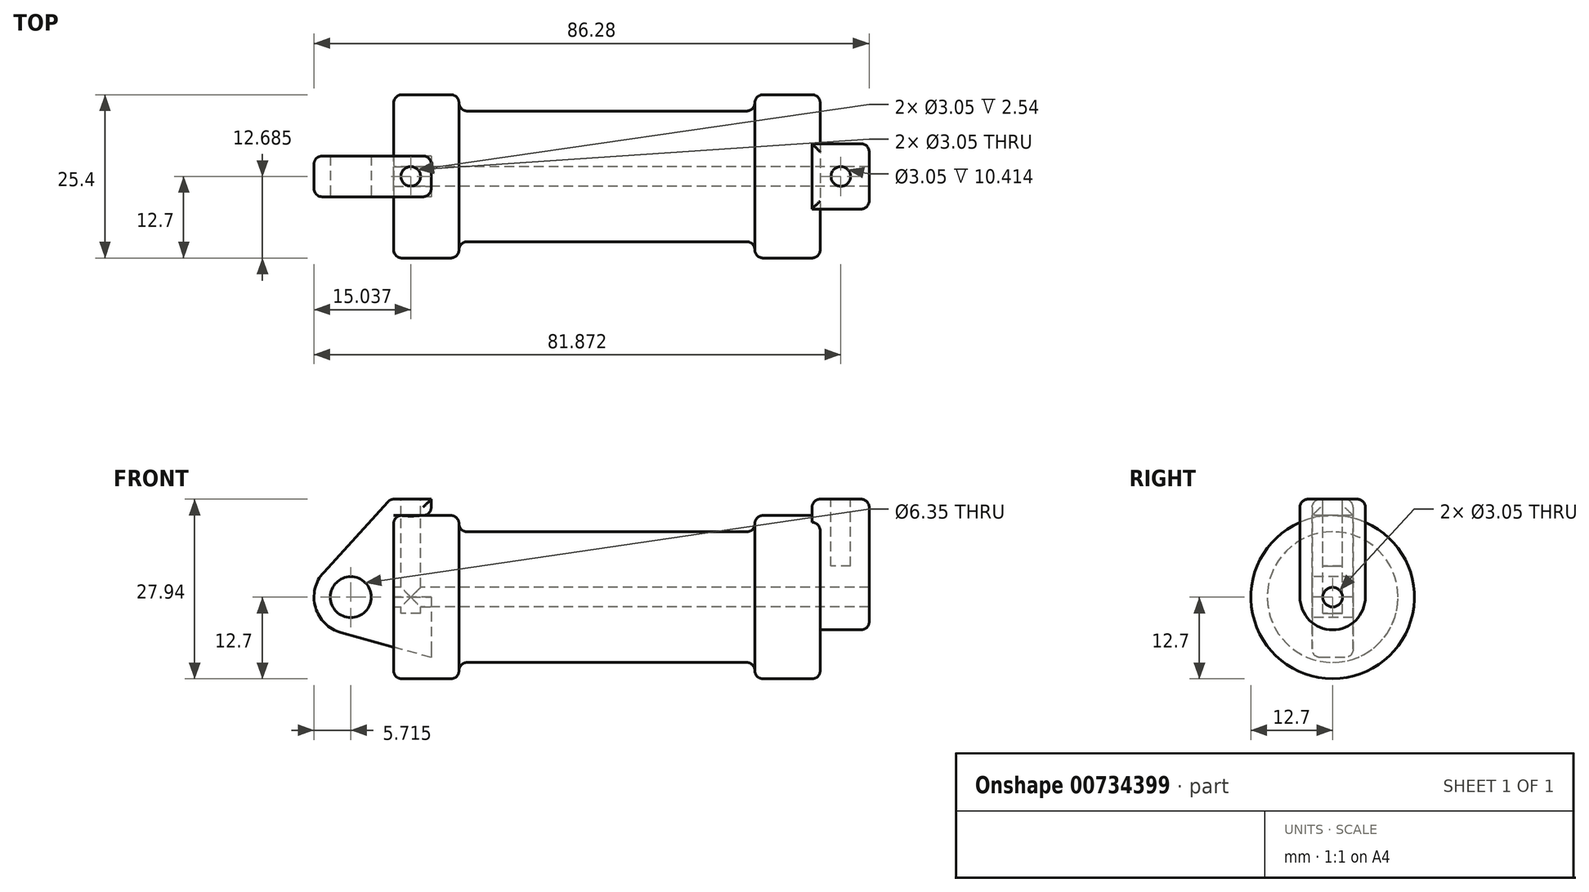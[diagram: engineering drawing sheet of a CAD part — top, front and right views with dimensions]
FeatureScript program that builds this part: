
annotation { "Feature Type Name" : "Feature", "Feature Type Description" : "" }
export const myFeature = defineFeature(function(context is Context, id is Id, definition is map)
    precondition{}
    {
        {
            var Q0;
            Q0=qCreatedBy(makeId("Front.planeOp"),FACE);
            var sketch = newSketch(context, id + "F0", { "sketchPlane" : qUnion([Q0])});
            skLineSegment(sketch, "E0", {"start": v(0, 0) * mm, "end": v(0, 12.7) * mm});
            skLineSegment(sketch, "E1", {"start": v(0, 12.7) * mm, "end": v(10.16, 12.7) * mm});
            skLineSegment(sketch, "E2", {"start": v(10.16, 12.7) * mm, "end": v(10.16, 10.16) * mm});
            skLineSegment(sketch, "E3", {"start": v(10.16, 10.16) * mm, "end": v(56.13, 10.16) * mm});
            skLineSegment(sketch, "E4", {"start": v(56.13, 10.16) * mm, "end": v(56.13, 12.7) * mm});
            skLineSegment(sketch, "E5", {"start": v(56.13, 12.7) * mm, "end": v(66.3, 12.7) * mm});
            skLineSegment(sketch, "E6", {"start": v(66.3, 12.7) * mm, "end": v(66.3, 0) * mm});
            skLineSegment(sketch, "E7", {"start": v(66.3, 0) * mm, "end": v(0, 0) * mm});
            skLineSegment(sketch, "E8", {"start": v(5.84, 15.24) * mm, "end": v(-0.5, 15.24) * mm});
            skLineSegment(sketch, "E9", {"start": v(-0.5, 15.24) * mm, "end": v(-10.88, 3.85) * mm});
            skLineSegment(sketch, "E10", {"start": v(0, 0) * mm, "end": v(-6.65, 0) * mm});
            skCircle(sketch, "E11", {"center": v(-6.65, 0) * mm, "radius": 5.72 * mm});
            skCircle(sketch, "E12", {"center": v(-6.65, 0) * mm, "radius": 3.18 * mm});
            skLineSegment(sketch, "E13", {"start": v(5.84, 15.24) * mm, "end": v(5.84, -9.4) * mm});
            skLineSegment(sketch, "E14", {"start": v(5.84, -9.4) * mm, "end": v(-8.18, -5.5) * mm});
            skSolve(sketch);
        }
        {
            var Q0;
            {var subQ0=sQuery(id+"F0.wireOp",EDGE,"E0");Q0=makeQuery(id+"F0.imprint","IMPRINT",FACE,{"disambiguationData":[TD([[makeQuery(id+"F0.imprint","IMPRINT",EDGE,{"derivedFrom":subQ0}),-1.0]])]});}
            var Q1;
            {var subQ0=sQuery(id+"F0.wireOp",EDGE,"E2");Q1=makeQuery(id+"F0.imprint","IMPRINT",FACE,{"disambiguationData":[TD([[makeQuery(id+"F0.imprint","IMPRINT",EDGE,{"derivedFrom":subQ0}),-1.0]])]});}
            var Q2;
            Q2=sQuery(id+"F0.wireOp",EDGE,"E7");
            revolve(context, id + "F1", {"surfaceOperationType" : NewSurfaceOperationType.NEW, "entities" : qUnion([Q0, Q1]), "axis" : qUnion([Q2]), "revolveType" : RevolveType.FULL});
        }
        {
            var Q0;
            {var subQ0=sQuery(id+"F0.wireOp",EDGE,"E14");Q0=makeQuery(id+"F0.imprint","IMPRINT",FACE,{"disambiguationData":[TD([[makeQuery(id+"F0.imprint","IMPRINT",EDGE,{"derivedFrom":subQ0}),-1.0]])]});}
            var Q1;
            {var subQ5=sQuery(id+"F0.wireOp",EDGE,"E12");Q1=makeQuery(id+"F0.imprint","IMPRINT",FACE,{"disambiguationData":[TD([[makeQuery(id+"F0.imprint","IMPRINT",EDGE,{"derivedFrom":subQ5}),-1.0]])]});}
            var Q2;
            {var subQ1=sQuery(id+"F0.wireOp",EDGE,"E0");Q2=makeQuery(id+"F0.imprint","IMPRINT",FACE,{"disambiguationData":[TD([[makeQuery(id+"F0.imprint","IMPRINT",EDGE,{"derivedFrom":subQ1}),1.0]])]});}
            extrude(context, id + "F2", {"entities" : qUnion([Q0, Q1, Q2]), "endBound" : BoundingType.SYMMETRIC, "oppositeDirection" : true, "depth" : 6.35 * mm, "offsetDistance" : 25.4 * mm});
        }
        {
            var Q0;
            Q0=makeQuery(id+"F1.opRevolve","SWEPT_FACE",FACE,{"disambiguationData":[OSD([sQuery(id+"F0.wireOp",EDGE,"E6")])]});
            var sketch = newSketch(context, id + "F3", { "sketchPlane" : qUnion([Q0])});
            skCircle(sketch, "E15", {"center": v(0, 0) * mm, "radius": 1.52 * mm});
            skCircle(sketch, "E16", {"center": v(0, 0) * mm, "radius": 5.08 * mm});
            skLineSegment(sketch, "E17", {"start": v(0, 0) * mm, "end": v(-5.08, 0) * mm});
            skLineSegment(sketch, "E18", {"start": v(-5.08, 0) * mm, "end": v(-5.08, 15.24) * mm});
            skLineSegment(sketch, "E19", {"start": v(5.08, 0) * mm, "end": v(5.08, 15.24) * mm});
            skLineSegment(sketch, "E20", {"start": v(-5.08, 15.24) * mm, "end": v(5.08, 15.24) * mm});
            skSolve(sketch);
        }
        {
            var Q0;
            {var subQ0=sQuery(id+"F3.wireOp",EDGE,"E20");Q0=makeQuery(id+"F3.imprint","IMPRINT",FACE,{"disambiguationData":[TD([[makeQuery(id+"F3.imprint","IMPRINT",EDGE,{"derivedFrom":subQ0}),-1.0]])]});}
            extrude(context, id + "F4", {"entities" : qUnion([Q0]), "operationType" : NewBodyOperationType.ADD, "oppositeDirection" : true, "depth" : 1.27 * mm, "offsetDistance" : 25.4 * mm});
        }
        {
            var Q0;
            Q0 = qSketchRegion(id + "F3", true);
            extrude(context, id + "F5", {"entities" : qUnion([Q0]), "operationType" : NewBodyOperationType.ADD, "depth" : 7.62 * mm, "offsetDistance" : 25.4 * mm});
        }
        {
            var Q0;
            {var subQ0=sQuery(id+"F0.wireOp",EDGE,"E6");Q0=makeQuery(id+"F5.boolean.opBoolean","SPLIT",FACE,{"disambiguationData":[TD([makeQuery(id+"F5.opExtrude","SWEPT_FACE",FACE,{"disambiguationData":[OSD([sQuery(id+"F3.wireOp",EDGE,"E15")])]})])],"derivedFrom":makeQuery(id+"F4.boolean.opBoolean","MERGE",FACE,{"derivedFrom":[makeQuery(id+"F1.opRevolve","SWEPT_FACE",FACE,{"disambiguationData":[OSD([subQ0])]}),makeQuery(id+"F4.opExtrude","CAP_FACE",FACE,{"disambiguationData":[OSD([sQuery(id+"F0.wireOp",EDGE,"E5"),subQ0,sQuery(id+"F3.wireOp",EDGE,"E18"),sQuery(id+"F3.wireOp",EDGE,"E19"),sQuery(id+"F3.wireOp",EDGE,"E20")])],"isStart":true})]})});}
            var Q1;
            Q1=makeQuery(id+"F1.opRevolve","SWEPT_BODY",BODY,{"disambiguationData":[OSD([sQuery(id+"F0.wireOp",EDGE,"E0"),sQuery(id+"F0.wireOp",EDGE,"E1"),sQuery(id+"F0.wireOp",EDGE,"E2"),sQuery(id+"F0.wireOp",EDGE,"E3"),sQuery(id+"F0.wireOp",EDGE,"E4"),sQuery(id+"F0.wireOp",EDGE,"E5"),sQuery(id+"F0.wireOp",EDGE,"E6"),sQuery(id+"F0.wireOp",EDGE,"E7")])]});
            extrude(context, id + "F6", {"entities" : qUnion([Q0]), "operationType" : NewBodyOperationType.REMOVE, "endBound" : BoundingType.UP_TO_BODY, "oppositeDirection" : true, "depth" : 25.4 * mm, "endBoundEntityBody" : qUnion([Q1]), "offsetDistance" : 25.4 * mm});
        }
        {
            var Q0;
            {var subQ0=sQuery(id+"F3.wireOp",EDGE,"E20");Q0=makeQuery(id+"F5.boolean.opBoolean","MERGE",FACE,{"derivedFrom":[makeQuery(id+"F4.opExtrude","SWEPT_FACE",FACE,{"disambiguationData":[OSD([subQ0])]}),makeQuery(id+"F5.opExtrude","SWEPT_FACE",FACE,{"disambiguationData":[OSD([subQ0])]})]});}
            var sketch = newSketch(context, id + "F7", { "sketchPlane" : qUnion([Q0])});
            skSolve(sketch);
        }
        {
            var Q0;
            {var subQ0=sQuery(id+"F3.wireOp",EDGE,"E20");Q0=makeQuery(id+"F7.imprint","IMPRINT",FACE,{"disambiguationData":[TD([[makeQuery(id+"F7.imprint","IMPRINT",EDGE,{"derivedFrom":makeQuery(id+"F4.opExtrude","CAP_EDGE",EDGE,{"disambiguationData":[OSD([subQ0])],"isStart":false})}),-1.0]])]});}
            var sketch = newSketch(context, id + "F8", { "sketchPlane" : qUnion([Q0])});
            skCircle(sketch, "E21", {"center": v(69.5, -0.02) * mm, "radius": 1.52 * mm});
            skSolve(sketch);
        }
        {
            var Q0;
            Q0=makeQuery(id+"F8.imprint","IMPRINT",FACE,{"disambiguationData":[TD([[makeQuery(id+"F8.imprint","IMPRINT",EDGE,{"derivedFrom":sQuery(id+"F8.wireOp",EDGE,"E21")}),1.0]])]});
            extrude(context, id + "F9", {"entities" : qUnion([Q0]), "operationType" : NewBodyOperationType.REMOVE, "oppositeDirection" : true, "depth" : 10.4 * mm, "offsetDistance" : 25.4 * mm});
        }
        {
            var Q0;
            Q0=makeQuery(id+"F2.opExtrude","SWEPT_FACE",FACE,{"disambiguationData":[OSD([sQuery(id+"F0.wireOp",EDGE,"E8")])]});
            var sketch = newSketch(context, id + "F10", { "sketchPlane" : qUnion([Q0])});
            skCircle(sketch, "E22", {"center": v(2.67, 0) * mm, "radius": 1.52 * mm});
            skPoint(sketch, "E22.centerSnap0", {"position": v(2.67, 3.18) * mm});
            skPoint(sketch, "E22.centerSnap1", {"position": v(5.84, 0) * mm});
            skSolve(sketch);
        }
        {
            var Q0;
            Q0 = qSketchRegion(id + "F10", true);
            extrude(context, id + "F11", {"entities" : qUnion([Q0]), "operationType" : NewBodyOperationType.REMOVE, "oppositeDirection" : true, "depth" : 17.78 * mm, "offsetDistance" : 25.4 * mm});
        }
        {
            var Q0;
            Q0=makeQuery(id+"F1.opRevolve","SWEPT_EDGE",EDGE,{"disambiguationData":[OSD([sQuery(id+"F0.wireOp",EDGE,"E0"),sQuery(id+"F0.wireOp",EDGE,"E1")])]});
            var Q1;
            Q1=makeQuery(id+"F1.opRevolve","SWEPT_EDGE",EDGE,{"disambiguationData":[OSD([sQuery(id+"F0.wireOp",EDGE,"E1"),sQuery(id+"F0.wireOp",EDGE,"E2")])]});
            var Q2;
            Q2=makeQuery(id+"F2.opExtrude","CAP_EDGE",EDGE,{"disambiguationData":[OSD([sQuery(id+"F0.wireOp",EDGE,"E9")])],"isStart":true});
            var Q3;
            Q3=makeQuery(id+"F2.opExtrude","CAP_EDGE",EDGE,{"disambiguationData":[OSD([sQuery(id+"F0.wireOp",EDGE,"E9")])],"isStart":false});
            var Q4;
            Q4=makeQuery(id+"F2.opExtrude","SWEPT_EDGE",EDGE,{"disambiguationData":[OSD([sQuery(id+"F0.wireOp",EDGE,"E9"),sQuery(id+"F0.wireOp",EDGE,"E11")])]});
            var Q5;
            Q5=makeQuery(id+"F2.opExtrude","SWEPT_EDGE",EDGE,{"disambiguationData":[OSD([sQuery(id+"F0.wireOp",EDGE,"E8"),sQuery(id+"F0.wireOp",EDGE,"E9")])]});
            var Q6;
            Q6=makeQuery(id+"F2.opExtrude","CAP_EDGE",EDGE,{"disambiguationData":[OSD([sQuery(id+"F0.wireOp",EDGE,"E8")])],"isStart":true});
            var Q7;
            Q7=makeQuery(id+"F2.opExtrude","CAP_EDGE",EDGE,{"disambiguationData":[OSD([sQuery(id+"F0.wireOp",EDGE,"E8")])],"isStart":false});
            var Q8;
            Q8=makeQuery(id+"F2.opExtrude","SWEPT_EDGE",EDGE,{"disambiguationData":[OSD([sQuery(id+"F0.wireOp",EDGE,"E1"),sQuery(id+"F0.wireOp",EDGE,"E13")])]});
            var Q9;
            {var subQ0=sQuery(id+"F0.wireOp",EDGE,"E13");Q9=makeQuery(id+"F2.opExtrude","CAP_EDGE",EDGE,{"disambiguationData":[OSD([subQ0]),TDD([makeQuery(id+"F0.imprint","IMPRINT",EDGE,{"disambiguationData":[TD([[makeQuery(id+"F0.imprint","INTERSECT",VERTEX,{"derivedFrom":[sQuery(id+"F0.wireOp",EDGE,"E8"),subQ0]}),-1.0]])],"derivedFrom":subQ0})])],"isStart":true});}
            var Q10;
            {var subQ0=sQuery(id+"F0.wireOp",EDGE,"E13");Q10=makeQuery(id+"F2.opExtrude","CAP_EDGE",EDGE,{"disambiguationData":[OSD([subQ0]),TDD([makeQuery(id+"F0.imprint","IMPRINT",EDGE,{"disambiguationData":[TD([[makeQuery(id+"F0.imprint","INTERSECT",VERTEX,{"derivedFrom":[sQuery(id+"F0.wireOp",EDGE,"E8"),subQ0]}),-1.0]])],"derivedFrom":subQ0})])],"isStart":false});}
            var Q11;
            Q11=makeQuery(id+"F2.opExtrude","SWEPT_EDGE",EDGE,{"disambiguationData":[OSD([sQuery(id+"F0.wireOp",EDGE,"E11"),sQuery(id+"F0.wireOp",EDGE,"E14")])]});
            var Q12;
            Q12=makeQuery(id+"F2.opExtrude","CAP_EDGE",EDGE,{"disambiguationData":[OSD([sQuery(id+"F0.wireOp",EDGE,"E14")])],"isStart":true});
            var Q13;
            Q13=makeQuery(id+"F2.opExtrude","CAP_EDGE",EDGE,{"disambiguationData":[OSD([sQuery(id+"F0.wireOp",EDGE,"E14")])],"isStart":false});
            var Q14;
            Q14=makeQuery(id+"F2.opExtrude","CAP_EDGE",EDGE,{"disambiguationData":[OSD([sQuery(id+"F0.wireOp",EDGE,"E11")])],"isStart":false});
            var Q15;
            Q15=makeQuery(id+"F2.opExtrude","CAP_EDGE",EDGE,{"disambiguationData":[OSD([sQuery(id+"F0.wireOp",EDGE,"E11")])],"isStart":true});
            fillet(context, id + "F12", {"entities" : qUnion([Q0, Q1, Q2, Q3, Q4, Q5, Q6, Q7, Q8, Q9, Q10, Q11, Q12, Q13, Q14, Q15]), "radius" : 1.27 * mm, "tangentPropagation" : true, "allowEdgeOverflow" : false});
        }
        {
            var Q0;
            Q0=makeQuery(id+"F1.opRevolve","SWEPT_EDGE",EDGE,{"disambiguationData":[OSD([sQuery(id+"F0.wireOp",EDGE,"E5"),sQuery(id+"F0.wireOp",EDGE,"E6")])]});
            var Q1;
            Q1=makeQuery(id+"F1.opRevolve","SWEPT_EDGE",EDGE,{"disambiguationData":[OSD([sQuery(id+"F0.wireOp",EDGE,"E4"),sQuery(id+"F0.wireOp",EDGE,"E5")])]});
            var Q2;
            Q2=makeQuery(id+"F5.opExtrude","CAP_EDGE",EDGE,{"disambiguationData":[OSD([sQuery(id+"F3.wireOp",EDGE,"E20")])],"isStart":false});
            var Q3;
            Q3=makeQuery(id+"F5.opExtrude","CAP_EDGE",EDGE,{"disambiguationData":[OSD([sQuery(id+"F3.wireOp",EDGE,"E18")])],"isStart":false});
            var Q4;
            Q4=makeQuery(id+"F5.opExtrude","SWEPT_EDGE",EDGE,{"disambiguationData":[OSD([sQuery(id+"F3.wireOp",EDGE,"E16"),sQuery(id+"F3.wireOp",EDGE,"E18")])]});
            var Q5;
            {var subQ0=sQuery(id+"F3.wireOp",EDGE,"E20");var subQ1=sQuery(id+"F3.wireOp",EDGE,"E18");Q5=makeQuery(id+"F5.boolean.opBoolean","MERGE",EDGE,{"derivedFrom":[makeQuery(id+"F4.opExtrude","SWEPT_EDGE",EDGE,{"disambiguationData":[OSD([subQ1,subQ0])]}),makeQuery(id+"F5.opExtrude","SWEPT_EDGE",EDGE,{"disambiguationData":[OSD([subQ1,subQ0])]})]});}
            var Q6;
            Q6=makeQuery(id+"F4.opExtrude","CAP_EDGE",EDGE,{"disambiguationData":[OSD([sQuery(id+"F3.wireOp",EDGE,"E20")])],"isStart":false});
            var Q7;
            {var subQ0=sQuery(id+"F3.wireOp",EDGE,"E20");var subQ1=sQuery(id+"F3.wireOp",EDGE,"E19");Q7=makeQuery(id+"F5.boolean.opBoolean","MERGE",EDGE,{"derivedFrom":[makeQuery(id+"F4.opExtrude","SWEPT_EDGE",EDGE,{"disambiguationData":[OSD([subQ1,subQ0])]}),makeQuery(id+"F5.opExtrude","SWEPT_EDGE",EDGE,{"disambiguationData":[OSD([subQ1,subQ0])]})]});}
            var Q8;
            Q8=makeQuery(id+"F1.opRevolve","SWEPT_FACE",FACE,{"disambiguationData":[OSD([sQuery(id+"F0.wireOp",EDGE,"E3")])]});
            fillet(context, id + "F13", {"entities" : qUnion([Q0, Q1, Q2, Q3, Q4, Q5, Q6, Q7, Q8]), "radius" : 1.27 * mm, "tangentPropagation" : true, "allowEdgeOverflow" : false});
        }
    });
